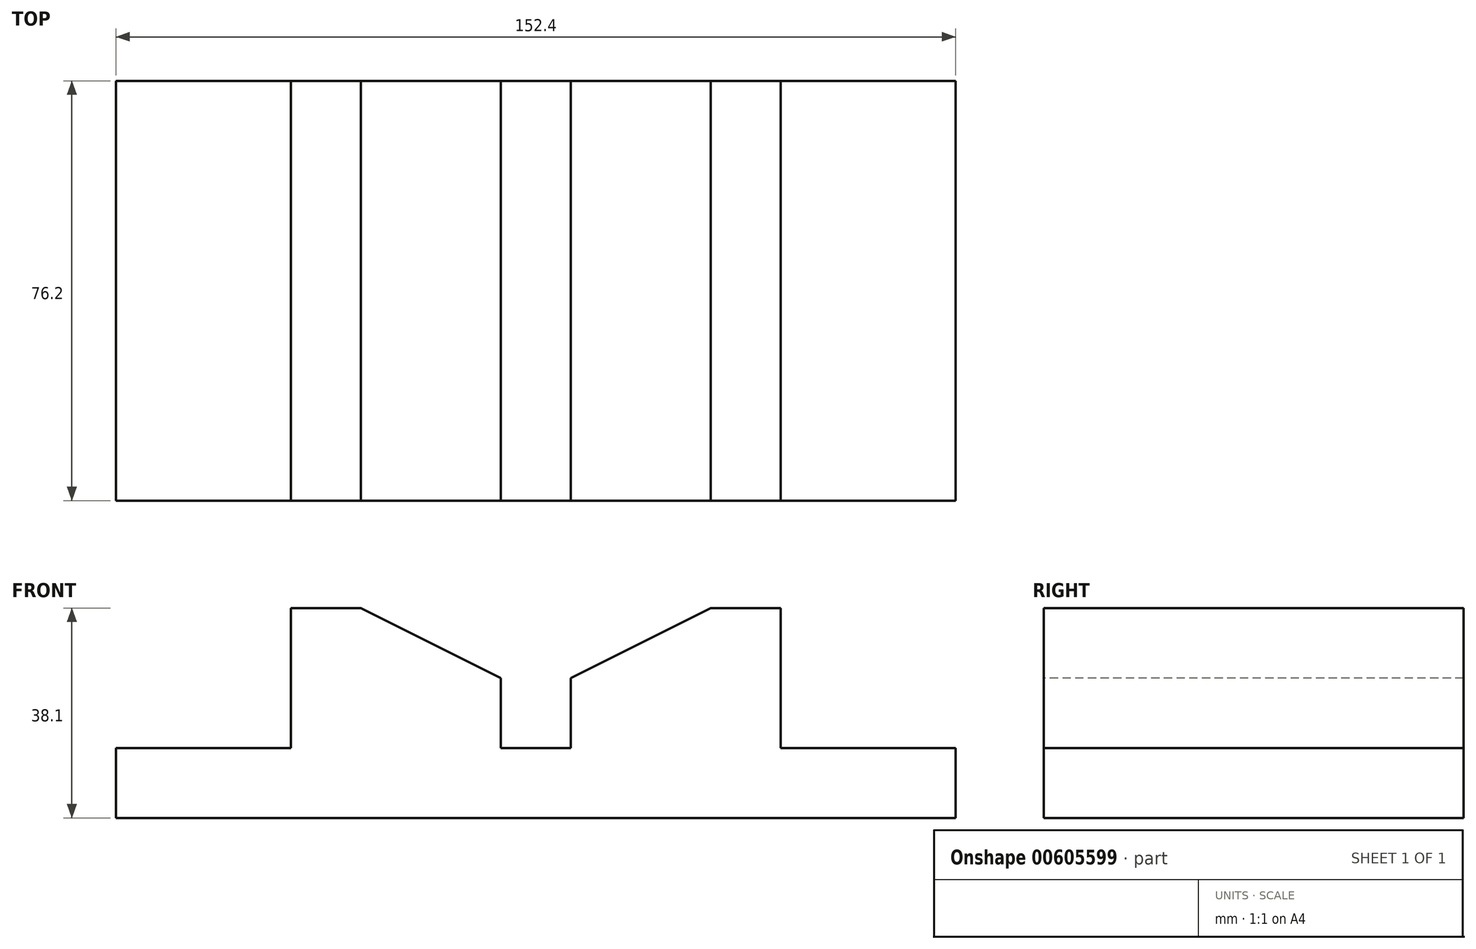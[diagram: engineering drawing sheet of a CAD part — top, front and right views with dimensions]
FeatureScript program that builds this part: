
annotation { "Feature Type Name" : "Feature", "Feature Type Description" : "" }
export const myFeature = defineFeature(function(context is Context, id is Id, definition is map)
    precondition{}
    {
        {
            var Q0;
            Q0=qCreatedBy(makeId("Front.planeOp"),FACE);
            var sketch = newSketch(context, id + "F0", { "sketchPlane" : qUnion([Q0])});
            skLineSegment(sketch, "E0", {"start": v(0, 0) * mm, "end": v(152.4, 0) * mm});
            skLineSegment(sketch, "E1", {"start": v(0, 0) * mm, "end": v(0, 12.7) * mm});
            skLineSegment(sketch, "E2", {"start": v(0, 12.7) * mm, "end": v(31.75, 12.7) * mm});
            skLineSegment(sketch, "E3", {"start": v(31.75, 12.7) * mm, "end": v(31.75, 38.1) * mm});
            skLineSegment(sketch, "E4", {"start": v(31.75, 38.1) * mm, "end": v(44.45, 38.1) * mm});
            skLineSegment(sketch, "E5", {"start": v(69.85, 12.7) * mm, "end": v(69.85, 25.4) * mm});
            skLineSegment(sketch, "E6", {"start": v(69.85, 25.4) * mm, "end": v(44.45, 38.1) * mm});
            skLineSegment(sketch, "E7", {"start": v(69.85, 12.7) * mm, "end": v(82.55, 12.7) * mm});
            skLineSegment(sketch, "E8", {"start": v(82.55, 12.7) * mm, "end": v(82.55, 25.4) * mm});
            skLineSegment(sketch, "E9", {"start": v(152.4, 0) * mm, "end": v(152.4, 12.7) * mm});
            skLineSegment(sketch, "E10", {"start": v(152.4, 12.7) * mm, "end": v(120.65, 12.7) * mm});
            skLineSegment(sketch, "E11", {"start": v(120.65, 12.7) * mm, "end": v(120.65, 38.1) * mm});
            skLineSegment(sketch, "E12", {"start": v(120.65, 38.1) * mm, "end": v(107.95, 38.1) * mm});
            skLineSegment(sketch, "E13", {"start": v(107.95, 38.1) * mm, "end": v(82.55, 25.4) * mm});
            skSolve(sketch);
        }
        {
            var Q0;
            Q0=makeQuery(id+"F0.imprint","IMPRINT",FACE,{"disambiguationData":[TD([[makeQuery(id+"F0.imprint","IMPRINT",EDGE,{"derivedFrom":sQuery(id+"F0.wireOp",EDGE,"E0")}),1.0]])]});
            extrude(context, id + "F1", {"entities" : qUnion([Q0]), "oppositeDirection" : true, "depth" : 76.2 * mm, "offsetDistance" : 25.4 * mm});
        }
    });
